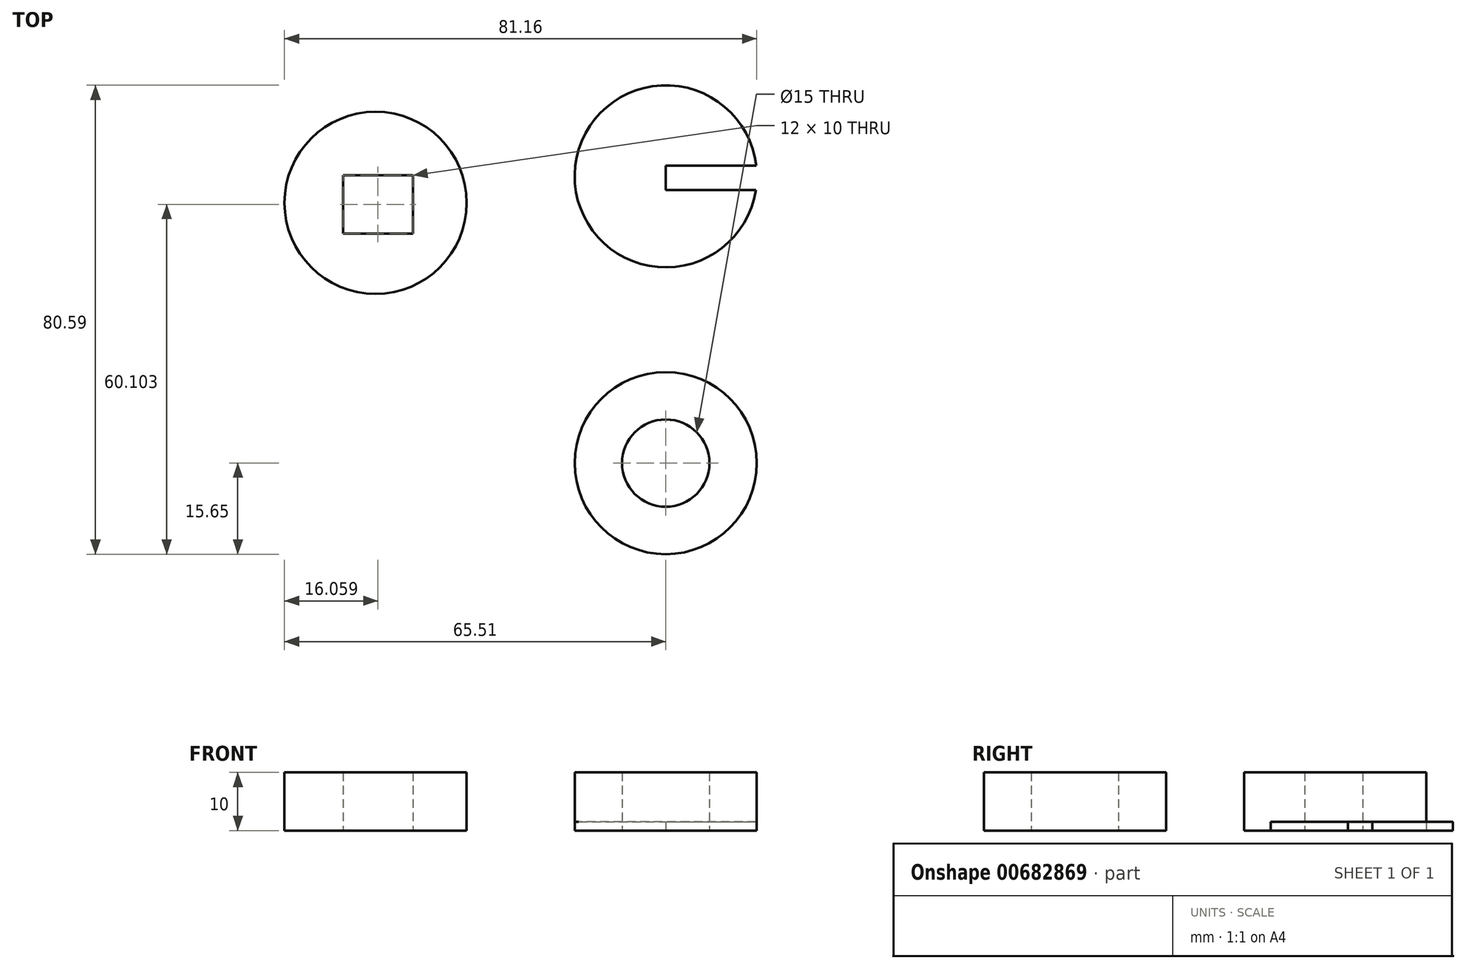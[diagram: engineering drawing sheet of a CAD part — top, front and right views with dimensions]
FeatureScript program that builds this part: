
annotation { "Feature Type Name" : "Feature", "Feature Type Description" : "" }
export const myFeature = defineFeature(function(context is Context, id is Id, definition is map)
    precondition{}
    {
        {
            var Q0;
            Q0=qCreatedBy(makeId("Top.planeOp"),FACE);
            var sketch = newSketch(context, id + "F0", { "sketchPlane" : qUnion([Q0])});
            skCircle(sketch, "E0", {"center": v(0, 0) * mm, "radius": 15.65 * mm});
            skCircle(sketch, "E1", {"center": v(0, 0) * mm, "radius": 7.5 * mm});
            skSolve(sketch);
        }
        {
            var Q0;
            Q0 = qSketchRegion(id + "F0", true);
            extrude(context, id + "F1", {"entities" : qUnion([Q0]), "depth" : 10 * mm, "offsetDistance" : 25 * mm});
        }
        {
            var Q0;
            Q0=qCreatedBy(makeId("Top.planeOp"),FACE);
            var sketch = newSketch(context, id + "F2", { "sketchPlane" : qUnion([Q0])});
            skCircle(sketch, "E2", {"center": v(-49.86, 44.73) * mm, "radius": 15.65 * mm});
            skLineSegment(sketch, "E3.bottom", {"start": v(-55.45, 49.45) * mm, "end": v(-43.45, 49.45) * mm});
            skLineSegment(sketch, "E3.top", {"start": v(-55.45, 39.45) * mm, "end": v(-43.45, 39.45) * mm});
            skLineSegment(sketch, "E3.left", {"start": v(-55.45, 49.45) * mm, "end": v(-55.45, 39.45) * mm});
            skLineSegment(sketch, "E3.right", {"start": v(-43.45, 49.45) * mm, "end": v(-43.45, 39.45) * mm});
            skSolve(sketch);
        }
        {
            var Q0;
            Q0 = qSketchRegion(id + "F2", true);
            extrude(context, id + "F3", {"entities" : qUnion([Q0]), "depth" : 10 * mm, "offsetDistance" : 25 * mm});
        }
        {
            var Q0;
            Q0=qCreatedBy(makeId("Top.planeOp"),FACE);
            var sketch = newSketch(context, id + "F4", { "sketchPlane" : qUnion([Q0])});
            skArc(sketch, "E4", {"start": v(15.55, 51.1) * mm, "mid": v(-15.65, 49.58) * mm, "end": v(15.47, 46.9) * mm});
            skLineSegment(sketch, "E5.bottom", {"start": v(0, 51.1) * mm, "end": v(15.55, 51.1) * mm});
            skLineSegment(sketch, "E5.top", {"start": v(0, 46.9) * mm, "end": v(15.47, 46.9) * mm});
            skLineSegment(sketch, "E5.left", {"start": v(0, 51.1) * mm, "end": v(0, 46.9) * mm});
            skSolve(sketch);
        }
        {
            var Q0;
            Q0=makeQuery(id+"F4.imprint","IMPRINT",FACE,{"disambiguationData":[TD([[makeQuery(id+"F4.imprint","IMPRINT",EDGE,{"derivedFrom":sQuery(id+"F4.wireOp",EDGE,"E4")}),1.0]])]});
            extrude(context, id + "F5", {"entities" : qUnion([Q0]), "depth" : 1.5 * mm, "offsetDistance" : 25 * mm});
        }
    });
